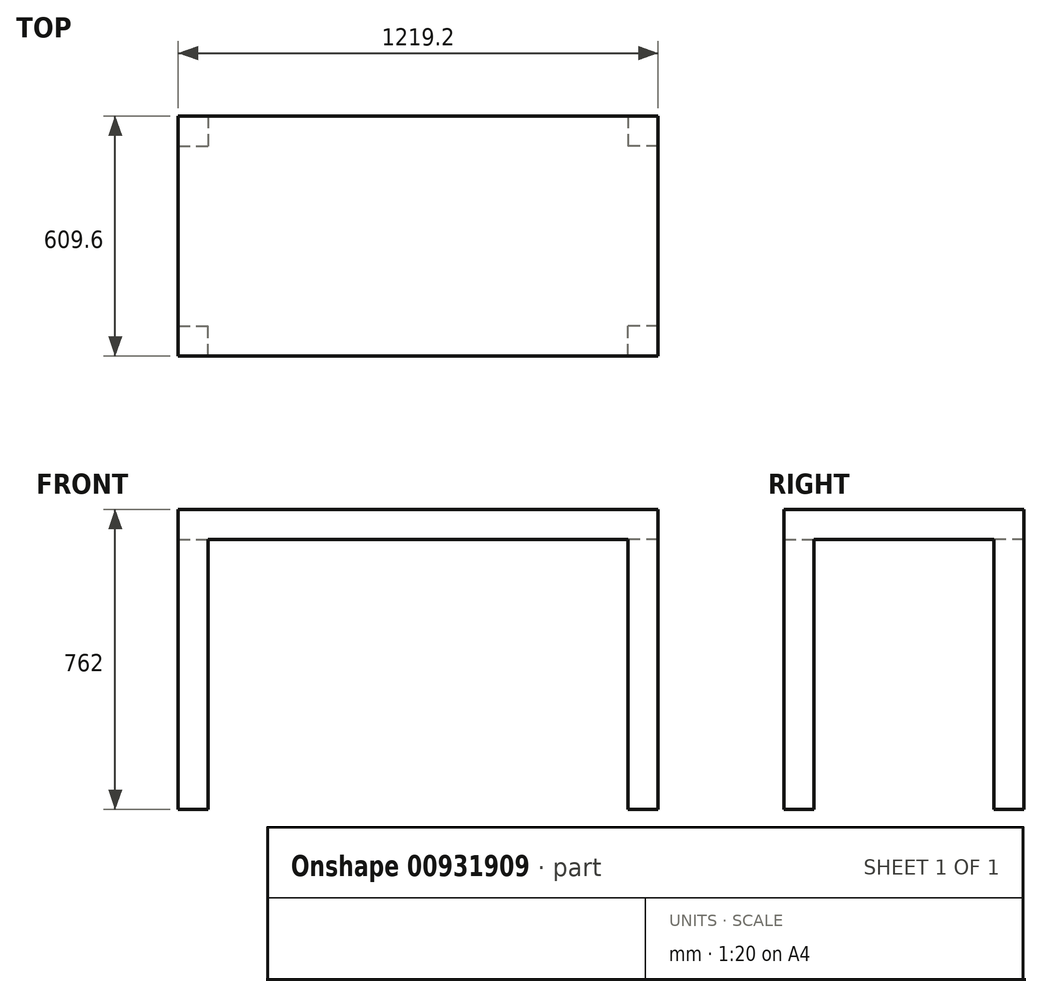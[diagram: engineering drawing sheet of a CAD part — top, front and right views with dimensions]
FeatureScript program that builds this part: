
annotation { "Feature Type Name" : "Feature", "Feature Type Description" : "" }
export const myFeature = defineFeature(function(context is Context, id is Id, definition is map)
    precondition{}
    {
        {
            var Q0;
            Q0=qCreatedBy(makeId("Top.planeOp"),FACE);
            var sketch = newSketch(context, id + "F0", { "sketchPlane" : qUnion([Q0])});
            skLineSegment(sketch, "E0.bottom", {"start": v(0, 0) * mm, "end": v(1219.2, 0) * mm});
            skLineSegment(sketch, "E0.top", {"start": v(0, -609.6) * mm, "end": v(1219.2, -609.6) * mm});
            skLineSegment(sketch, "E0.left", {"start": v(0, 0) * mm, "end": v(0, -609.6) * mm});
            skLineSegment(sketch, "E0.right", {"start": v(1219.2, 0) * mm, "end": v(1219.2, -609.6) * mm});
            skLineSegment(sketch, "E1.bottom", {"start": v(0, 0) * mm, "end": v(76.2, 0) * mm});
            skLineSegment(sketch, "E1.top", {"start": v(0, -76.2) * mm, "end": v(76.2, -76.2) * mm});
            skLineSegment(sketch, "E1.left", {"start": v(0, 0) * mm, "end": v(0, -76.2) * mm});
            skLineSegment(sketch, "E1.right", {"start": v(76.2, 0) * mm, "end": v(76.2, -76.2) * mm});
            skLineSegment(sketch, "E2.bottom", {"start": v(1219.2, 0) * mm, "end": v(1143, 0) * mm});
            skLineSegment(sketch, "E2.top", {"start": v(1219.2, -76.2) * mm, "end": v(1143, -76.2) * mm});
            skLineSegment(sketch, "E2.left", {"start": v(1219.2, 0) * mm, "end": v(1219.2, -76.2) * mm});
            skLineSegment(sketch, "E2.right", {"start": v(1143, 0) * mm, "end": v(1143, -76.2) * mm});
            skLineSegment(sketch, "E3.bottom", {"start": v(0, -609.6) * mm, "end": v(76.2, -609.6) * mm});
            skLineSegment(sketch, "E3.top", {"start": v(0, -533.4) * mm, "end": v(76.2, -533.4) * mm});
            skLineSegment(sketch, "E3.left", {"start": v(0, -609.6) * mm, "end": v(0, -533.4) * mm});
            skLineSegment(sketch, "E3.right", {"start": v(76.2, -609.6) * mm, "end": v(76.2, -533.4) * mm});
            skLineSegment(sketch, "E4.bottom", {"start": v(1219.2, -609.6) * mm, "end": v(1143, -609.6) * mm});
            skLineSegment(sketch, "E4.top", {"start": v(1219.2, -533.4) * mm, "end": v(1143, -533.4) * mm});
            skLineSegment(sketch, "E4.left", {"start": v(1219.2, -609.6) * mm, "end": v(1219.2, -533.4) * mm});
            skLineSegment(sketch, "E4.right", {"start": v(1143, -609.6) * mm, "end": v(1143, -533.4) * mm});
            skSolve(sketch);
        }
        {
            var Q0;
            Q0 = qSketchRegion(id + "F0", true);
            extrude(context, id + "F1", {"entities" : qUnion([Q0]), "oppositeDirection" : true, "depth" : 76.2 * mm, "offsetDistance" : 25.4 * mm});
        }
        {
            var Q0;
            {var subQ4=sQuery(id+"F0.wireOp",EDGE,"E1.top");Q0=makeQuery(id+"F0.imprint","IMPRINT",FACE,{"disambiguationData":[TD([[makeQuery(id+"F0.imprint","IMPRINT",EDGE,{"derivedFrom":subQ4}),1.0]])]});}
            var Q1;
            {var subQ4=sQuery(id+"F0.wireOp",EDGE,"E3.top");Q1=makeQuery(id+"F0.imprint","IMPRINT",FACE,{"disambiguationData":[TD([[makeQuery(id+"F0.imprint","IMPRINT",EDGE,{"derivedFrom":subQ4}),-1.0]])]});}
            var Q2;
            {var subQ4=sQuery(id+"F0.wireOp",EDGE,"E2.top");Q2=makeQuery(id+"F0.imprint","IMPRINT",FACE,{"disambiguationData":[TD([[makeQuery(id+"F0.imprint","IMPRINT",EDGE,{"derivedFrom":subQ4}),-1.0]])]});}
            var Q3;
            {var subQ4=sQuery(id+"F0.wireOp",EDGE,"E4.top");Q3=makeQuery(id+"F0.imprint","IMPRINT",FACE,{"disambiguationData":[TD([[makeQuery(id+"F0.imprint","IMPRINT",EDGE,{"derivedFrom":subQ4}),1.0]])]});}
            extrude(context, id + "F2", {"entities" : qUnion([Q0, Q1, Q2, Q3]), "operationType" : NewBodyOperationType.ADD, "oppositeDirection" : true, "depth" : 762 * mm, "offsetDistance" : 25.4 * mm});
        }
    });
